# Revit family: CADS_Vent-Axia_MechEquip_Fan_BIFA_450_3Ph2P - SUPPLY
name_source: partatom
category: Mechanical Equipment
units: mm (PartAtom-declared; Revit-internal decimal feet)

## family parameters
Always vertical = Yes
Cut with Voids When Loaded = No
OmniClass Number = 23.75.00.00
OmniClass Title = Climate Control (HVAC)
Part Type = Normal
Room Calculation Point = No
Round Connector Dimension = Use Diameter
Shared = No
Work Plane-Based = No

## types (12) — shared parameters
AirflowRateRange = 0.0 L/s
AssemblyPlace = UNKNOWN
AssetType = FIXED
DurationUnit = Year
ExteriorInsulation = No
Fitting Type = Ignore
GrossWeight = 0.00 kg
HasProtectiveEarth = No
IfcExportAs = IfcFanType
IsExtendedWarranty = No
ManufacturerAddress = Fleming Way
Crawley 
RH10 9YX
NominalDiameter = 450 mm  [stored 1.47638 ft]
NominalHeight = 450 mm  [stored 1.47638 ft]
NominalLength = 625 mm  [stored 2.05052 ft]
NominalWidth = 450 mm  [stored 1.47638 ft]
Quantity = 1
RatedCurrent = 0 A
RatedVoltage = 0 V
Status = New
WarrantyGuarantor = Vent-Axia Limited
WorkingPressure = 0.0 Pa
zero-valued in all types: CADS_Index, CADS_Usage, Default Elevation, ExpectedServiceLife, NumberOfPoles

## per-type parameters (varying)
| type | ModelReference |
| BIFA453210 | BIF 450MM 3PH 2P 10DEG |
| BIFA453212 | BIF 450MM 3PH 2P 12DEG |
| BIFA453214 | BIF 450MM 3PH 2P 14DEG |
| BIFA453216 | BIF 450MM 3PH 2P 16DEG |
| BIFA453218 | BIF 450MM 3PH 2P 18DEG |
| BIFA453220 | BIF 450MM 3PH 2P 20DEG |
| BIFA453222 | BIF 450MM 3PH 2P 22DEG |
| BIFA453224 | BIF 450MM 3PH 2P 24DEG |
| BIFA453226 | BIF 450MM 3PH 2P 26DEG |
| BIFA453228 | BIF 450MM 3PH 2P 28DEG |
| BIFA453230 | BIF 450MM 3PH 2P 30DEG |
| BIFA453232 | BIF 450MM 3PH 2P 32DEG |

note: column(s) folded — value = type name in every type: ModelNumber

note: [stored X ft] marks values corroborated as IEEE doubles in the binary element streams (Revit-internal decimal feet)

## geometry (parser evidence)
native form markers: Sweep x11
no freeform markers — native parametric forms only
